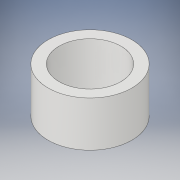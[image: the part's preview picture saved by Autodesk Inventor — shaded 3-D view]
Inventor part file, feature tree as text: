
AUTODESK INVENTOR PART (.ipt)
format: ipt  version: 2017.1 (Build 211199000, 199)  size: 99,840 bytes
history: native  units: in
note: dims shown in document units (in); Inventor stores cm internally (conversion verified against a paired STEP export)
features: extrude x2, sketch x2
ambient origin geometry x8: Origin, YZ Plane, XZ Plane, XY Plane, X Axis, Y Axis, Z Axis, Center Point
bodies: Solid1 (feature_tree)
feature tree (4):
  extrude  "Extrusion1"  Depth=0.28in TaperAngle=0.0deg
  extrude  "Extrusion2"  Depth=0.345in TaperAngle=0.0deg
  sketch  "Sketch1"  dims[d0=0.518in d1=0.28in d2=0.0in]
  sketch  "Sketch2"  dims[d3=0.382in d4=0.345in d5=0.0in]
